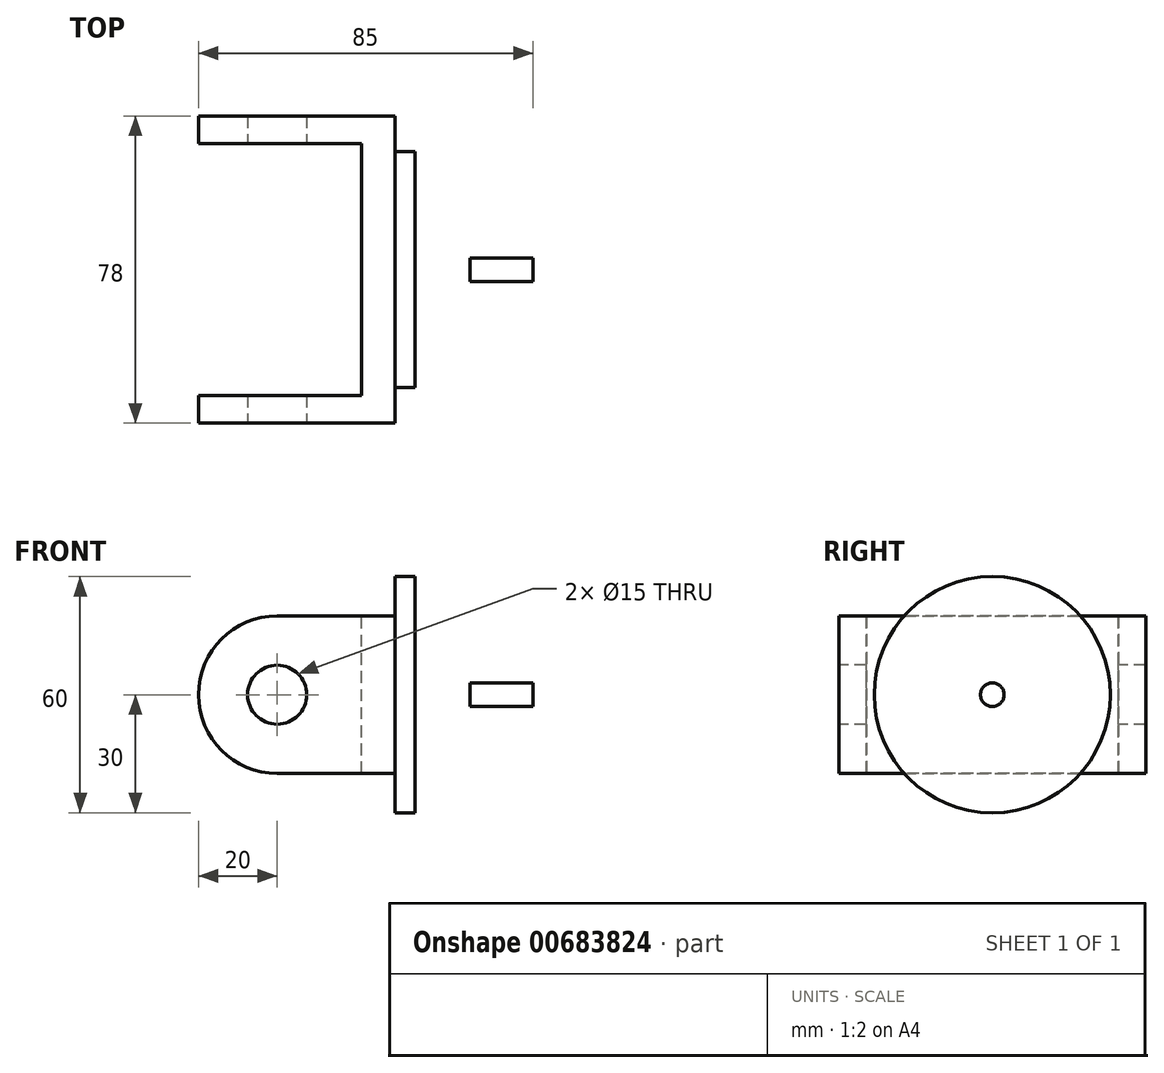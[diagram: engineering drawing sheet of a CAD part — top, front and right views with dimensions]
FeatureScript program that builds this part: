
annotation { "Feature Type Name" : "Feature", "Feature Type Description" : "" }
export const myFeature = defineFeature(function(context is Context, id is Id, definition is map)
    precondition{}
    {
        {
            var Q0;
            Q0=qCreatedBy(makeId("Front.planeOp"),FACE);
            var sketch = newSketch(context, id + "F0", { "sketchPlane" : qUnion([Q0])});
            skLineSegment(sketch, "E0.bottom", {"start": v(0, 0) * mm, "end": v(35, 0) * mm});
            skLineSegment(sketch, "E0.top", {"start": v(0, 7.5) * mm, "end": v(35, 7.5) * mm});
            skLineSegment(sketch, "E0.left", {"start": v(0, 0) * mm, "end": v(0, 7.5) * mm});
            skLineSegment(sketch, "E0.right", {"start": v(35, 0) * mm, "end": v(35, 7.5) * mm});
            skLineSegment(sketch, "E1.bottom", {"start": v(0, 0) * mm, "end": v(5, 0) * mm});
            skLineSegment(sketch, "E1.top", {"start": v(0, 30) * mm, "end": v(5, 30) * mm});
            skLineSegment(sketch, "E1.left", {"start": v(0, 0) * mm, "end": v(0, 30) * mm});
            skLineSegment(sketch, "E1.right", {"start": v(5, 0) * mm, "end": v(5, 30) * mm});
            skLineSegment(sketch, "E2.MirrorCS", {"start": v(0, 0) * mm, "end": v(0, -7.5) * mm});
            skLineSegment(sketch, "E3.MirrorCS", {"start": v(0, -7.5) * mm, "end": v(35, -7.5) * mm});
            skLineSegment(sketch, "E4.MirrorCS", {"start": v(35, 0) * mm, "end": v(35, -7.5) * mm});
            skLineSegment(sketch, "E5.MirrorCS", {"start": v(0, -30) * mm, "end": v(5, -30) * mm});
            skLineSegment(sketch, "E6.MirrorCS", {"start": v(0, 0) * mm, "end": v(0, -30) * mm});
            skLineSegment(sketch, "E7.MirrorCS", {"start": v(5, 0) * mm, "end": v(5, -30) * mm});
            skLineSegment(sketch, "E8.bottom", {"start": v(0, 20) * mm, "end": v(-30, 20) * mm});
            skLineSegment(sketch, "E8.top", {"start": v(0, -20) * mm, "end": v(-30, -20) * mm});
            skLineSegment(sketch, "E8.left", {"start": v(0, 20) * mm, "end": v(0, -20) * mm});
            skLineSegment(sketch, "E9", {"start": v(-30, 0) * mm, "end": v(0, 0) * mm});
            skCircle(sketch, "E10", {"center": v(-30, 0) * mm, "radius": 20 * mm});
            skLineSegment(sketch, "E11.bottom", {"start": v(19, 3) * mm, "end": v(35, 3) * mm});
            skLineSegment(sketch, "E11.top", {"start": v(19, 0) * mm, "end": v(35, 0) * mm});
            skLineSegment(sketch, "E11.left", {"start": v(19, 3) * mm, "end": v(19, 0) * mm});
            skLineSegment(sketch, "E11.right", {"start": v(35, 3) * mm, "end": v(35, 0) * mm});
            skLineSegment(sketch, "E12.MirrorCS", {"start": v(35, -3) * mm, "end": v(35, 0) * mm});
            skLineSegment(sketch, "E13.MirrorCS", {"start": v(19, -3) * mm, "end": v(35, -3) * mm});
            skLineSegment(sketch, "E14.MirrorCS", {"start": v(19, -3) * mm, "end": v(19, 0) * mm});
            skSolve(sketch);
        }
        {
            var Q0;
            {var subQ1=sQuery(id+"F0.wireOp",EDGE,"E0.bottom");Q0=makeQuery(id+"F0.imprint","IMPRINT",FACE,{"disambiguationData":[TD([[makeQuery(id+"F0.imprint","IMPRINT",EDGE,{"derivedFrom":subQ1}),1.0]])]});}
            var Q1;
            {var subQ5=sQuery(id+"F0.wireOp",EDGE,"E1.bottom");Q1=makeQuery(id+"F0.imprint","IMPRINT",FACE,{"disambiguationData":[TD([[makeQuery(id+"F0.imprint","IMPRINT",EDGE,{"derivedFrom":subQ5}),1.0]])]});}
            var Q2;
            {var subQ1=sQuery(id+"F0.wireOp",EDGE,"E1.top");Q2=makeQuery(id+"F0.imprint","IMPRINT",FACE,{"disambiguationData":[TD([[makeQuery(id+"F0.imprint","IMPRINT",EDGE,{"derivedFrom":subQ1}),-1.0]])]});}
            var Q3;
            Q3=sQuery(id+"F0.wireOp",EDGE,"E0.bottom");
            revolve(context, id + "F1", {"entities" : qUnion([Q0, Q1, Q2]), "axis" : qUnion([Q3]), "revolveType" : RevolveType.FULL});
        }
        {
            var Q0;
            {var subQ0=sQuery(id+"F0.wireOp",EDGE,"E10");var subQ1=makeQuery(id+"F0.imprint","INTERSECT",VERTEX,{"derivedFrom":[sQuery(id+"F0.wireOp",EDGE,"E8.bottom"),subQ0]});Q0=makeQuery(id+"F0.imprint","IMPRINT",FACE,{"disambiguationData":[TD([[makeQuery(id+"F0.imprint","IMPRINT",EDGE,{"disambiguationData":[TD([[subQ1,1.0]])],"derivedFrom":subQ0}),1.0]])]});}
            var Q1;
            {var subQ6=sQuery(id+"F0.wireOp",EDGE,"E8.bottom");Q1=makeQuery(id+"F0.imprint","IMPRINT",FACE,{"disambiguationData":[TD([[makeQuery(id+"F0.imprint","IMPRINT",EDGE,{"derivedFrom":subQ6}),1.0]])]});}
            var Q2;
            {var subQ2=sQuery(id+"F0.wireOp",EDGE,"E8.top");Q2=makeQuery(id+"F0.imprint","IMPRINT",FACE,{"disambiguationData":[TD([[makeQuery(id+"F0.imprint","IMPRINT",EDGE,{"derivedFrom":subQ2}),-1.0]])]});}
            extrude(context, id + "F2", {"entities" : qUnion([Q0, Q1, Q2]), "operationType" : NewBodyOperationType.ADD, "endBound" : BoundingType.SYMMETRIC, "depth" : 78 * mm, "offsetDistance" : 25 * mm});
        }
        {
            var Q0;
            Q0=qCreatedBy(makeId("Top.planeOp"),FACE);
            var sketch = newSketch(context, id + "F3", { "sketchPlane" : qUnion([Q0])});
            skLineSegment(sketch, "E15", {"start": v(-50, -39) * mm, "end": v(0, -39) * mm});
            skLineSegment(sketch, "E16", {"start": v(-50, 39) * mm, "end": v(0, 39) * mm});
            skLineSegment(sketch, "E17", {"start": v(-50, -39) * mm, "end": v(-50, 39) * mm});
            skLineSegment(sketch, "E18", {"start": v(0, 20) * mm, "end": v(0, 30) * mm});
            skLineSegment(sketch, "E19", {"start": v(0, -30) * mm, "end": v(0, -20) * mm});
            skLineSegment(sketch, "E20", {"start": v(5, -7.5) * mm, "end": v(35, -7.5) * mm});
            skLineSegment(sketch, "E21", {"start": v(35, 7.5) * mm, "end": v(5, 7.5) * mm});
            skLineSegment(sketch, "E22.bottom", {"start": v(-50, 32) * mm, "end": v(-8.55, 32) * mm});
            skLineSegment(sketch, "E22.top", {"start": v(-50, 0) * mm, "end": v(-8.55, 0) * mm});
            skLineSegment(sketch, "E22.left", {"start": v(-50, 32) * mm, "end": v(-50, 0) * mm});
            skLineSegment(sketch, "E22.right", {"start": v(-8.55, 32) * mm, "end": v(-8.55, 0) * mm});
            skLineSegment(sketch, "E23.MirrorCS", {"start": v(-8.55, -32) * mm, "end": v(-8.55, 0) * mm});
            skLineSegment(sketch, "E24.MirrorCS", {"start": v(-50, -32) * mm, "end": v(-50, 0) * mm});
            skLineSegment(sketch, "E25.MirrorCS", {"start": v(-50, -32) * mm, "end": v(-8.55, -32) * mm});
            skSolve(sketch);
        }
        {
            var Q0;
            Q0=qSketchRegion(id+"F3",true);
            extrude(context, id + "F4", {"entities" : qUnion([Q0]), "operationType" : NewBodyOperationType.REMOVE, "endBound" : BoundingType.SYMMETRIC, "oppositeDirection" : true, "depth" : 100 * mm, "offsetDistance" : 25 * mm});
        }
        {
            var Q0;
            Q0=makeQuery(id+"F2.opExtrude","CAP_FACE",FACE,{"disambiguationData":[OSD([sQuery(id+"F0.wireOp",EDGE,"E8.bottom"),sQuery(id+"F0.wireOp",EDGE,"E8.top"),sQuery(id+"F0.wireOp",EDGE,"E8.left"),sQuery(id+"F0.wireOp",EDGE,"E10")])],"isStart":false});
            var sketch = newSketch(context, id + "F5", { "sketchPlane" : qUnion([Q0])});
            skArc(sketch, "E26.0.0", {"start": v(-30, 20) * mm, "mid": v(-50, 0) * mm, "end": v(-30, -20) * mm});
            skLineSegment(sketch, "E26.0.1", {"start": v(-30, -20) * mm, "end": v(0, -20) * mm});
            skLineSegment(sketch, "E26.0.2", {"start": v(0, -20) * mm, "end": v(0, 20) * mm});
            skLineSegment(sketch, "E26.0.3", {"start": v(0, 20) * mm, "end": v(-30, 20) * mm});
            skCircle(sketch, "E27", {"center": v(-30, 0) * mm, "radius": 7.5 * mm});
            skSolve(sketch);
        }
        {
            var Q0;
            Q0=makeQuery(id+"F5.imprint","IMPRINT",FACE,{"disambiguationData":[TD([[makeQuery(id+"F5.imprint","IMPRINT",EDGE,{"derivedFrom":sQuery(id+"F5.wireOp",EDGE,"E27")}),1.0]])]});
            extrude(context, id + "F6", {"entities" : qUnion([Q0]), "operationType" : NewBodyOperationType.REMOVE, "endBound" : BoundingType.THROUGH_ALL, "oppositeDirection" : true, "depth" : 25 * mm, "offsetDistance" : 25 * mm});
        }
    });
